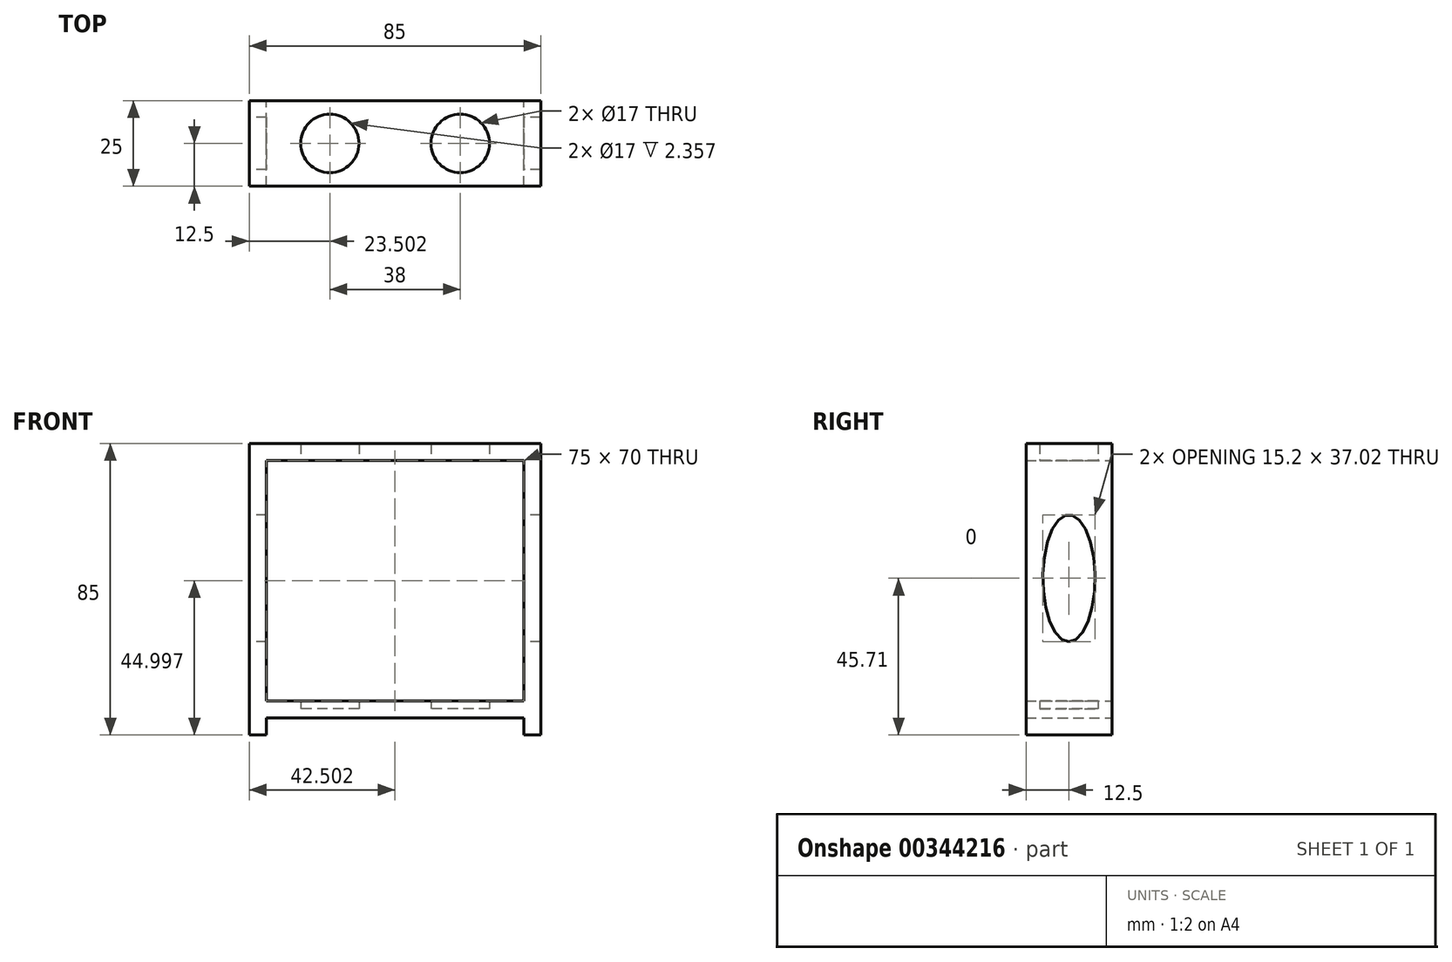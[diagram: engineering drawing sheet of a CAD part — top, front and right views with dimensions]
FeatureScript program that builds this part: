
annotation { "Feature Type Name" : "Feature", "Feature Type Description" : "" }
export const myFeature = defineFeature(function(context is Context, id is Id, definition is map)
    precondition{}
    {
        {
            var Q0;
            Q0=qCreatedBy(makeId("Front.planeOp"),FACE);
            var sketch = newSketch(context, id + "F0", { "sketchPlane" : qUnion([Q0])});
            skLineSegment(sketch, "E0.bottom", {"start": v(-50.8, 36.36) * mm, "end": v(-45.8, 36.36) * mm});
            skLineSegment(sketch, "E0.top", {"start": v(-50.8, -48.64) * mm, "end": v(-45.8, -48.64) * mm});
            skLineSegment(sketch, "E0.left", {"start": v(-50.8, 36.36) * mm, "end": v(-50.8, -48.64) * mm});
            skLineSegment(sketch, "E0.right", {"start": v(-45.8, 36.36) * mm, "end": v(-45.8, -48.64) * mm});
            skLineSegment(sketch, "E1.bottom", {"start": v(29.2, 36.36) * mm, "end": v(34.2, 36.36) * mm});
            skLineSegment(sketch, "E1.top", {"start": v(29.2, -48.64) * mm, "end": v(34.2, -48.64) * mm});
            skLineSegment(sketch, "E1.left", {"start": v(29.2, 36.36) * mm, "end": v(29.2, -48.64) * mm});
            skLineSegment(sketch, "E1.right", {"start": v(34.2, 36.36) * mm, "end": v(34.2, -48.64) * mm});
            skLineSegment(sketch, "E2", {"start": v(-45.8, 36.36) * mm, "end": v(29.2, 36.36) * mm});
            skLineSegment(sketch, "E3", {"start": v(-45.8, 31.36) * mm, "end": v(29.2, 31.36) * mm});
            skLineSegment(sketch, "E4", {"start": v(-45.8, -43.64) * mm, "end": v(29.2, -43.64) * mm});
            skLineSegment(sketch, "E5", {"start": v(-45.8, -38.64) * mm, "end": v(29.2, -38.64) * mm});
            skSolve(sketch);
        }
        {
            var Q0;
            {var subQ1=sQuery(id+"F0.wireOp",EDGE,"E0.bottom");Q0=makeQuery(id+"F0.imprint","IMPRINT",FACE,{"disambiguationData":[TD([[makeQuery(id+"F0.imprint","IMPRINT",EDGE,{"derivedFrom":subQ1}),-1.0]])]});}
            var Q1;
            {var subQ0=sQuery(id+"F0.wireOp",EDGE,"E2");Q1=makeQuery(id+"F0.imprint","IMPRINT",FACE,{"disambiguationData":[TD([[makeQuery(id+"F0.imprint","IMPRINT",EDGE,{"derivedFrom":subQ0}),-1.0]])]});}
            var Q2;
            {var subQ3=sQuery(id+"F0.wireOp",EDGE,"E1.bottom");Q2=makeQuery(id+"F0.imprint","IMPRINT",FACE,{"disambiguationData":[TD([[makeQuery(id+"F0.imprint","IMPRINT",EDGE,{"derivedFrom":subQ3}),-1.0]])]});}
            var Q3;
            {var subQ0=sQuery(id+"F0.wireOp",EDGE,"E4");Q3=makeQuery(id+"F0.imprint","IMPRINT",FACE,{"disambiguationData":[TD([[makeQuery(id+"F0.imprint","IMPRINT",EDGE,{"derivedFrom":subQ0}),1.0]])]});}
            extrude(context, id + "F1", {"entities" : qUnion([Q0, Q1, Q2, Q3]), "depth" : 25 * mm});
        }
        {
            var Q0;
            Q0=qCreatedBy(makeId("Right.planeOp"),FACE);
            var sketch = newSketch(context, id + "F2", { "sketchPlane" : qUnion([Q0])});
            skLineSegment(sketch, "E6.bottom", {"start": v(0, 36.32) * mm, "end": v(-25, 36.32) * mm});
            skLineSegment(sketch, "E6.top", {"start": v(0, -48.68) * mm, "end": v(-25, -48.68) * mm});
            skLineSegment(sketch, "E6.left", {"start": v(0, 36.32) * mm, "end": v(0, -48.68) * mm});
            skLineSegment(sketch, "E6.right", {"start": v(-25, 36.32) * mm, "end": v(-25, -48.68) * mm});
            skLineSegment(sketch, "E7", {"start": v(0, -38.68) * mm, "end": v(-25, -38.68) * mm});
            skLineSegment(sketch, "E8", {"start": v(0, 31.32) * mm, "end": v(-25, 31.32) * mm});
            skEllipse(sketch, "E9", {"center": v(-12.5, -2.93) * mm, "majorRadius": 18.5 * mm, "minorRadius": 7.6 * mm, "majorAxis": v(0, -1)});
            skLineSegment(sketch, "E10.bottom", {"start": v(-5, -48.68) * mm, "end": v(-20, -48.68) * mm});
            skLineSegment(sketch, "E10.top", {"start": v(-5, -38.68) * mm, "end": v(-20, -38.68) * mm});
            skLineSegment(sketch, "E10.left", {"start": v(-5, -48.68) * mm, "end": v(-5, -38.68) * mm});
            skLineSegment(sketch, "E10.right", {"start": v(-20, -48.68) * mm, "end": v(-20, -38.68) * mm});
            skLineSegment(sketch, "E11", {"start": v(0, -43.68) * mm, "end": v(-25, -43.68) * mm});
            skSolve(sketch);
        }
        {
            var Q0;
            {var subQ0=sQuery(id+"F2.wireOp",EDGE,"E10.bottom");Q0=makeQuery(id+"F2.imprint","IMPRINT",FACE,{"disambiguationData":[TD([[makeQuery(id+"F2.imprint","IMPRINT",EDGE,{"derivedFrom":subQ0}),-1.0]])]});}
            var Q1;
            Q1=makeQuery(id+"F2.imprint","IMPRINT",FACE,{"disambiguationData":[TD([[makeQuery(id+"F2.imprint","IMPRINT",EDGE,{"derivedFrom":sQuery(id+"F2.wireOp",EDGE,"E9")}),1.0]])]});
            extrude(context, id + "F3", {"entities" : qUnion([Q0, Q1]), "operationType" : NewBodyOperationType.REMOVE, "endBound" : BoundingType.SYMMETRIC, "depth" : 200 * mm});
        }
        {
            var Q0;
            Q0=qCreatedBy(makeId("Top.planeOp"),FACE);
            var sketch = newSketch(context, id + "F4", { "sketchPlane" : qUnion([Q0])});
            skCircle(sketch, "E12", {"center": v(10.7, -12.5) * mm, "radius": 8.5 * mm});
            skLineSegment(sketch, "E13.bottom", {"start": v(-50.8, 0) * mm, "end": v(34.2, 0) * mm});
            skLineSegment(sketch, "E13.top", {"start": v(-50.8, -25) * mm, "end": v(34.2, -25) * mm});
            skLineSegment(sketch, "E13.left", {"start": v(-50.8, 0) * mm, "end": v(-50.8, -25) * mm});
            skLineSegment(sketch, "E13.right", {"start": v(34.2, 0) * mm, "end": v(34.2, -25) * mm});
            skCircle(sketch, "E14", {"center": v(-27.3, -12.5) * mm, "radius": 8.5 * mm});
            skSolve(sketch);
        }
        {
            var Q0;
            Q0=makeQuery(id+"F4.imprint","IMPRINT",FACE,{"disambiguationData":[TD([[makeQuery(id+"F4.imprint","IMPRINT",EDGE,{"derivedFrom":sQuery(id+"F4.wireOp",EDGE,"E14")}),1.0]])]});
            var Q1;
            Q1=makeQuery(id+"F4.imprint","IMPRINT",FACE,{"disambiguationData":[TD([[makeQuery(id+"F4.imprint","IMPRINT",EDGE,{"derivedFrom":sQuery(id+"F4.wireOp",EDGE,"E12")}),1.0]])]});
            extrude(context, id + "F5", {"entities" : qUnion([Q0, Q1]), "operationType" : NewBodyOperationType.REMOVE, "endBound" : BoundingType.SYMMETRIC, "depth" : 82 * mm});
        }
    });
